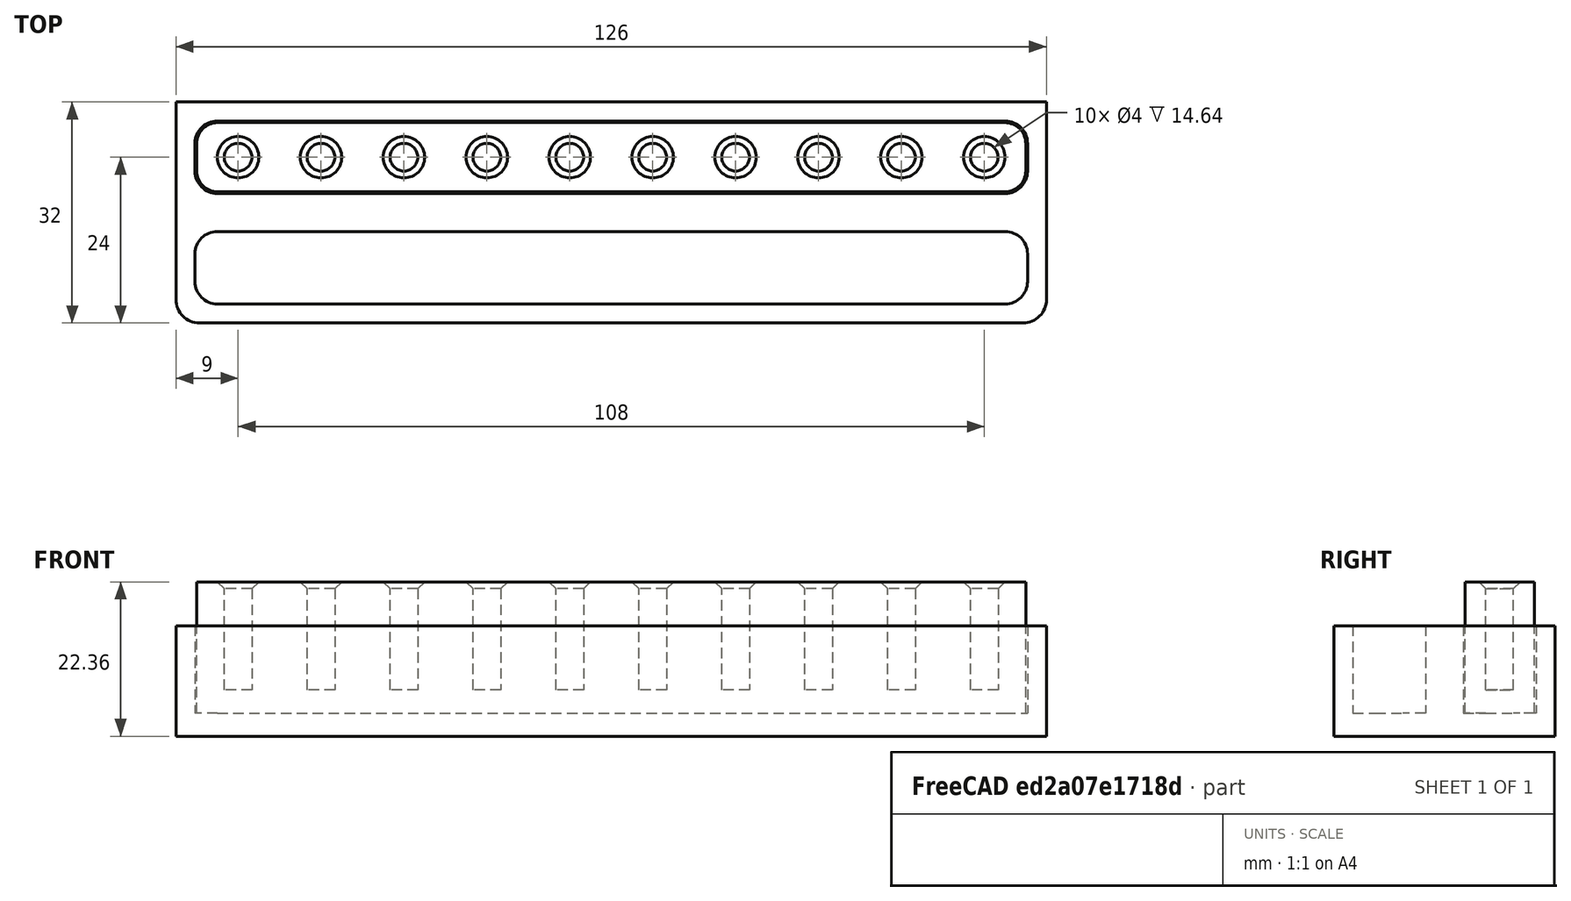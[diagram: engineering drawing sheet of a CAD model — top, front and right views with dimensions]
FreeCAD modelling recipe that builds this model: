
FCSTD DOCUMENT  (FreeCAD 0.19R24366 (Git))
Label: parametric-drill-bits-holder
License: All rights reserved
LicenseURL: http://en.wikipedia.org/wiki/All_rights_reserved
objects: Sketcher::SketchObject×4, Mesh::Feature×3, PartDesign::Pad×2, PartDesign::Plane×2, PartDesign::Pocket×2, PartDesign::Fillet×2, PartDesign::Body×2, Spreadsheet::Sheet×1, PartDesign::Chamfer×1, PartDesign::LinearPattern×1, Part::Refine×1, Part::Fillet×1, Part::MultiFuse×1, App::Part×1
note: 26 computed .brp shape members not serialized (recipe doc carries the construction recipe); baked Part::Feature solids carry a one-line shape summary decoded from their .brp

FEATURE [Spreadsheet::Sheet] Spreadsheet
  cells = A1=Gornji Deo (top part):; A3=duzina (length); B3(duzina)==120mm; A4=sirina (width); B4(sirina)==10mm; A5=visina (height); B5(visina)==19mm; D5=Tolerancija Stampaca  (printer tolerance); E5(tolerancija)==0.25mm; A6=okvir oko rupa (pad around holes); B6(okvir)==4mm; A7=precnik rupe (hole diameter); B7(diametar)==3.5mm + tolerancija * 2; A8=broj rupa u redu (number of holes); B8(broj_rupa)=10; A9=obaranje ivica (fillet diameter); B9(obaranje_ivice)==3mm; A12=Donji Deo (bottom part):; A14=duzina postolja (length); B14(duzina_postolja)==duzina + 6mm; A15=sirina postolja (width); B15(sirina_postolja)==sirina + 6mm; A16=visina postolja (height); B16(visina_postolja)==16mm
FEATURE [Sketcher::SketchObject] Sketch
  FullyConstrained = true
  MapMode = 5
  Support = -> [XY_Plane001]
  expr: Constraints[9] = Spreadsheet.sirina
  expr: Constraints[8] = Spreadsheet.duzina
  sketch-geometry (4):
    g0: LineSegment StartX=-60 StartY=5 StartZ=0 EndX=60 EndY=5 EndZ=0
    g1: LineSegment StartX=60 StartY=5 StartZ=0 EndX=60 EndY=-5 EndZ=0
    g2: LineSegment StartX=60 StartY=-5 StartZ=0 EndX=-60 EndY=-5 EndZ=0
    g3: LineSegment StartX=-60 StartY=-5 StartZ=0 EndX=-60 EndY=5 EndZ=0
  constraints (10):
    c: Coincident(g0,g1)
    c: Coincident(g1,g2)
    c: Coincident(g2,g3)
    c: Coincident(g3,g0)
    c: Horizontal(g2)
    c: Vertical(g3)
    c: Symmetric(g0,g0,g-2)
    c: Symmetric(g0,g1,g-1)
    c: DistanceX(g0,g0) = 120
    c: DistanceY(g2,g0) = 10
FEATURE [PartDesign::Pad] Pad
  Direction = (1,1,1)
  Length = 19
  Length2 = 100
  Profile = -> Sketch
  Type = 0
  expr: Length = Spreadsheet.visina
FEATURE [PartDesign::Plane] DatumPlane
  Length = 135.492
  MapMode = 5
  Placement = pos=(0,0,19) rot=(0,0,1;0rad)
  ResizeMode = 0
  Support = -> [Pad]
  Width = 65.4919
FEATURE [Sketcher::SketchObject] Sketch001
  FullyConstrained = true
  MapMode = 5
  Placement = pos=(0,0,19) rot=(0,0,1;0rad)
  Support = -> [DatumPlane]
  expr: Constraints[1] = Spreadsheet.duzina / 2 - Spreadsheet.diametar / 2 - Spreadsheet.okvir
  expr: Constraints[0] = Spreadsheet.diametar
  sketch-geometry (1):
    g0: Circle CenterX=-54 CenterY=0 CenterZ=0 NormalX=0 NormalY=0 NormalZ=1 AngleXU=0 Radius=2
  constraints (3):
    c: Diameter(g0) = 4
    c: DistanceX(g0,g-1) = 54
    c: PointOnObject(g0,g-1)
FEATURE [PartDesign::Pocket] Pocket
  BaseFeature = -> Pad
  Length = 15.64
  Length2 = 100
  Profile = -> Sketch001
  Type = 0
  expr: Length = Spreadsheet.visina - 3.36mm
FEATURE [Sketcher::SketchObject] Sketch002
  FullyConstrained = true
  MapMode = 5
  Support = -> [XY_Plane002]
  expr: Constraints[8] = Spreadsheet.duzina_postolja
  expr: Constraints[9] = Spreadsheet.sirina_postolja
  sketch-geometry (4):
    g0: LineSegment StartX=-63 StartY=8 StartZ=0 EndX=63 EndY=8 EndZ=0
    g1: LineSegment StartX=63 StartY=8 StartZ=0 EndX=63 EndY=-8 EndZ=0
    g2: LineSegment StartX=63 StartY=-8 StartZ=0 EndX=-63 EndY=-8 EndZ=0
    g3: LineSegment StartX=-63 StartY=-8 StartZ=0 EndX=-63 EndY=8 EndZ=0
  constraints (10):
    c: Coincident(g0,g1)
    c: Coincident(g1,g2)
    c: Coincident(g2,g3)
    c: Coincident(g3,g0)
    c: Horizontal(g2)
    c: Vertical(g3)
    c: Symmetric(g0,g0,g-2)
    c: Symmetric(g0,g1,g-1)
    c: DistanceX(g0,g0) = 126
    c: DistanceY(g1,g0) = 16
FEATURE [PartDesign::Pad] Pad001
  Direction = (1,1,1)
  Length = 16
  Length2 = 100
  Profile = -> Sketch002
  Type = 0
  expr: Length = Spreadsheet.visina_postolja
FEATURE [PartDesign::Plane] DatumPlane001
  Length = 141.875
  MapMode = 5
  Placement = pos=(0,0,16) rot=(0,0,1;0rad)
  ResizeMode = 0
  Support = -> [Pad001]
  Width = 65.8745
FEATURE [Sketcher::SketchObject] Sketch003
  FullyConstrained = true
  MapMode = 5
  Placement = pos=(0,0,16) rot=(0,0,1;0rad)
  Support = -> [DatumPlane001]
  expr: Constraints[8] = Spreadsheet.duzina + Spreadsheet.tolerancija * 2
  expr: Constraints[9] = Spreadsheet.sirina + Spreadsheet.tolerancija * 2
  sketch-geometry (4):
    g0: LineSegment StartX=-60.25 StartY=5.25 StartZ=0 EndX=60.25 EndY=5.25 EndZ=0
    g1: LineSegment StartX=60.25 StartY=5.25 StartZ=0 EndX=60.25 EndY=-5.25 EndZ=0
    g2: LineSegment StartX=60.25 StartY=-5.25 StartZ=0 EndX=-60.25 EndY=-5.25 EndZ=0
    g3: LineSegment StartX=-60.25 StartY=-5.25 StartZ=0 EndX=-60.25 EndY=5.25 EndZ=0
  constraints (10):
    c: Coincident(g0,g1)
    c: Coincident(g1,g2)
    c: Coincident(g2,g3)
    c: Coincident(g3,g0)
    c: Horizontal(g2)
    c: Vertical(g3)
    c: Symmetric(g0,g0,g-2)
    c: Symmetric(g0,g1,g-1)
    c: DistanceX(g0,g0) = 120.5
    c: DistanceY(g1,g0) = 10.5
FEATURE [PartDesign::Pocket] Pocket001
  BaseFeature = -> Pad001
  Length = 12.64
  Length2 = 100
  Profile = -> Sketch003
  Type = 0
  expr: Length = Spreadsheet.visina_postolja - 3.36mm
FEATURE [PartDesign::Fillet] Fillet001
  Base = -> Pocket001 [Edge17,Edge22,Edge20,Edge18]
  BaseFeature = -> Pocket001
  Radius = 3.25
  SupportTransform = false
  expr: Radius = Spreadsheet.obaranje_ivice + Spreadsheet.tolerancija
FEATURE [PartDesign::Body] Body001  label="Postolje"
  Group = -> [Sketch002,Pad001,DatumPlane001,Sketch003,Pocket001,Fillet001]
  Origin = -> Origin002
  Tip = -> Fillet001
FEATURE [PartDesign::Chamfer] Chamfer
  Angle = 45
  Base = -> Pocket [Edge13]
  BaseFeature = -> Pocket
  ChamferType = 0
  FlipDirection = false
  Size = 1
  Size2 = 1
  SupportTransform = false
FEATURE [PartDesign::LinearPattern] LinearPattern
  BaseFeature = -> Chamfer
  Direction = -> Sketch001 [H_Axis]
  Length = 108
  Occurrences = 10
  Originals = -> [Pocket,Chamfer]
  expr: Length = Spreadsheet.duzina - Spreadsheet.diametar - Spreadsheet.okvir * 2
  expr: Occurrences = Spreadsheet.broj_rupa
FEATURE [PartDesign::Fillet] Fillet
  Base = -> LinearPattern [Edge20,Edge16,Edge18,Edge15]
  BaseFeature = -> LinearPattern
  Radius = 3
  SupportTransform = false
  expr: Radius = Spreadsheet.obaranje_ivice
FEATURE [PartDesign::Body] Body  label="Drzac"
  Group = -> [Sketch,Pad,DatumPlane,Sketch001,Pocket,Chamfer,LinearPattern,Fillet]
  Origin = -> Origin001
  Placement = pos=(0,0,3.36) rot=(0,0,1;0rad)
  Tip = -> Fillet
FEATURE [Part::Refine] Body001003  label="Postolje003"
  Placement = pos=(0,-16,0) rot=(0,0,1;0rad)
  Source = -> Body001
  expr: .Placement.Base.y = Spreadsheet.sirina_postolja * -1
FEATURE [Part::Fillet] Fillet003  label="Postolje_2"
  Base = -> Body001003
  Edges = 2 edges r=3.4: [Edge32,Edge34]
FEATURE [Part::MultiFuse] Fusion  label="2_Spojena_Postolja"
  Shapes = -> [Body001,Fillet003]
FEATURE [App::Part] Part  label="Drzac burgija"
  Group = -> [Body,Body001,Body001003,Fillet003,Fusion]
  Origin = -> Origin
FEATURE [Mesh::Feature] Mesh  label="2_Spojena_Postolja (Meshed)"
FEATURE [Mesh::Feature] Mesh001  label="Drzac (Meshed)"
FEATURE [Mesh::Feature] Mesh002  label="Postolje_2 (Meshed)"
